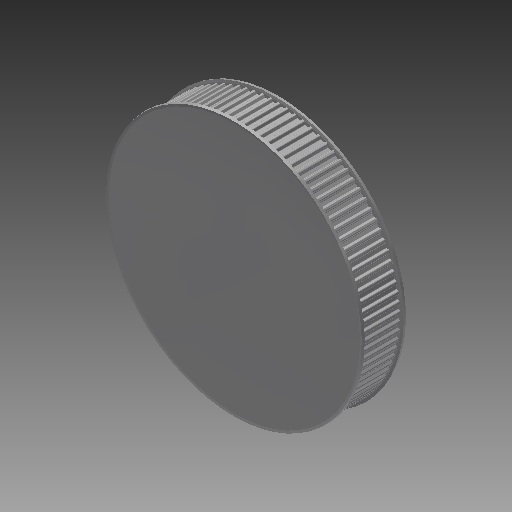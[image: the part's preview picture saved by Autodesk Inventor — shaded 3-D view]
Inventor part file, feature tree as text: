
AUTODESK INVENTOR PART (.ipt)
format: ipt  version: 2017 (Build 210142000, 142)  size: 1,161,216 bytes
history: native  units: mm (DEFAULTED — no unit token found)
features: other x3, extrude x2, fillet x1, pattern_circular x1
ambient origin geometry x8: Origin, YZ Plane, XZ Plane, XY Plane, X Axis, Y Axis, Z Axis, Center Point
bodies: Solid1 (feature_tree)
feature tree (7):
  other  "Pulley Sketch"
  extrude  "Base Body"  Depth=76.394373mm
  extrude  "Tooth"  Depth=0.3mm
  fillet  "Tooth Fillet"  Radius=0.75mm
  pattern_circular  "Teeth"  [2 undecoded]
  other  "Left flange"
  other  "Right flange"
note: 2 required parameter values undecoded (feature->parameter linkage not recoverable at this tier; creation-order binding heuristic only, values carry confidence <= 0.55)
